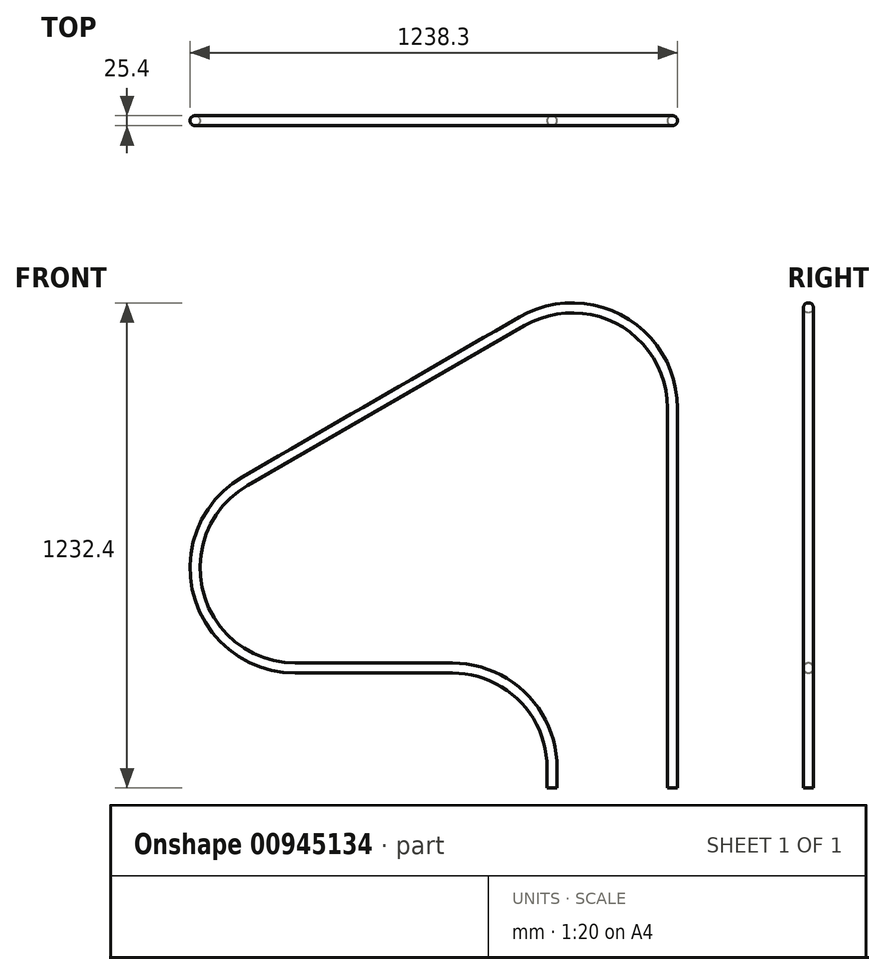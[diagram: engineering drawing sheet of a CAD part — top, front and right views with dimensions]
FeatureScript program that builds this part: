
annotation { "Feature Type Name" : "Feature", "Feature Type Description" : "" }
export const myFeature = defineFeature(function(context is Context, id is Id, definition is map)
    precondition{}
    {
        {
            var Q0;
            Q0=qCreatedBy(makeId("Front.planeOp"),FACE);
            var sketch = newSketch(context, id + "F0", { "sketchPlane" : qUnion([Q0])});
            skLineSegment(sketch, "E0", {"start": v(0, 0) * mm, "end": v(0, 965.2) * mm});
            skLineSegment(sketch, "E1", {"start": v(-381, 1185.17) * mm, "end": v(-1084.9, 778.77) * mm});
            skLineSegment(sketch, "E2", {"start": v(-957.9, 304.8) * mm, "end": v(-558.8, 304.8) * mm});
            skLineSegment(sketch, "E3", {"start": v(-304.8, 50.8) * mm, "end": v(-304.8, 0) * mm});
            skPoint(sketch, "E4.visualSharp", {"position": v(0, 1405.14) * mm});
            skArc(sketch, "E4.filletArc", {"start": v(0, 965.2) * mm, "mid": v(-127, 1185.17) * mm, "end": v(-381, 1185.17) * mm});
            skPoint(sketch, "E5.visualSharp", {"position": v(-1905.85, 304.8) * mm});
            skArc(sketch, "E5.filletArc", {"start": v(-1084.9, 778.77) * mm, "mid": v(-1203.25, 493.06) * mm, "end": v(-957.9, 304.8) * mm});
            skLineSegment(sketch, "E6", {"start": v(-592.27, 1219.2) * mm, "end": v(0, 1219.2) * mm, "construction": true});
            skPoint(sketch, "E7.visualSharp", {"position": v(-304.8, 304.8) * mm});
            skArc(sketch, "E7.filletArc", {"start": v(-304.8, 50.8) * mm, "mid": v(-379.2, 230.4) * mm, "end": v(-558.8, 304.8) * mm});
            skSolve(sketch);
        }
        {
            var Q0;
            Q0=qCreatedBy(makeId("Top.planeOp"),FACE);
            var sketch = newSketch(context, id + "F1", { "sketchPlane" : qUnion([Q0])});
            skCircle(sketch, "E8", {"center": v(0.5, 0.94) * mm, "radius": 12.7 * mm});
            skSolve(sketch);
        }
        {
            var Q0;
            Q0=makeQuery(id+"F1.imprint","IMPRINT",FACE,{"disambiguationData":[TD([[makeQuery(id+"F1.imprint","IMPRINT",EDGE,{"derivedFrom":sQuery(id+"F1.wireOp",EDGE,"E8")}),1.0]])]});
            var Q1;
            Q1 = qConstructionFilter(qBodyType(qCreatedBy(id + "F0" ,EDGE), BodyType.WIRE), ConstructionObject.NO);
            sweep(context, id + "F2", {"profiles" : qUnion([Q0]), "path" : qUnion([Q1])});
        }
    });
